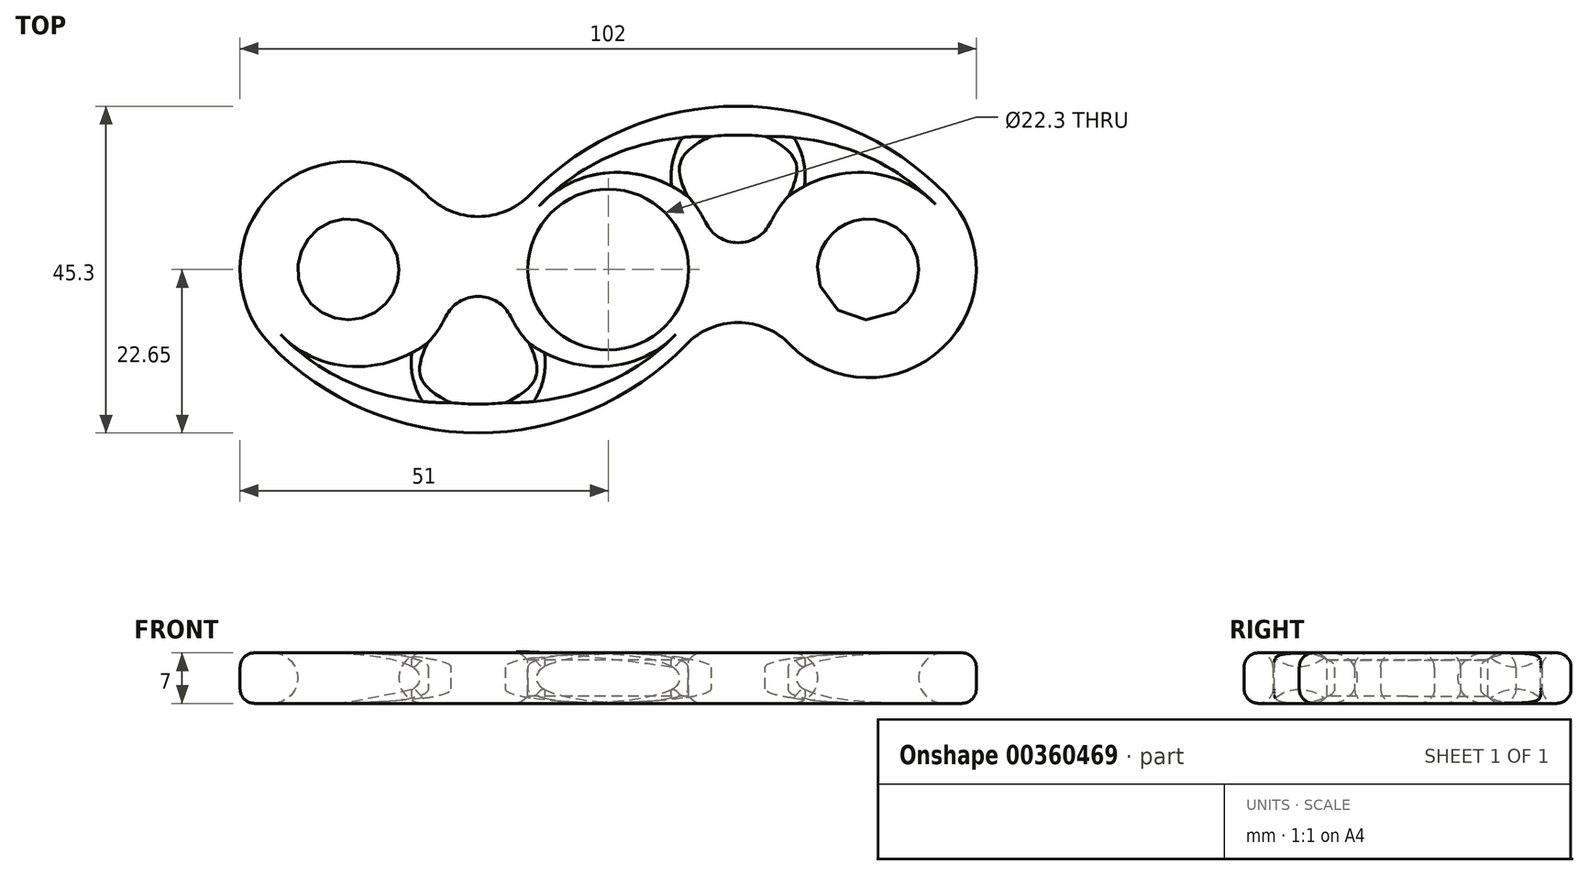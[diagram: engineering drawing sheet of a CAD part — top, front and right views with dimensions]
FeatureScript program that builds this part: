
annotation { "Feature Type Name" : "Feature", "Feature Type Description" : "" }
export const myFeature = defineFeature(function(context is Context, id is Id, definition is map)
    precondition{}
    {
        {
            var Q0;
            Q0=qCreatedBy(makeId("Top.planeOp"),FACE);
            var sketch = newSketch(context, id + "F0", { "sketchPlane" : qUnion([Q0])});
            skLineSegment(sketch, "E0", {"start": v(10.8, -10.4) * mm, "end": v(10.8, -10.4) * mm});
            skArc(sketch, "E1", {"start": v(-34.05, -14.87) * mm, "mid": v(-27.22, -12.16) * mm, "end": v(-22.5, -6.54) * mm});
            skArc(sketch, "E2", {"start": v(25.2, -10.4) * mm, "mid": v(46.4, -10.8) * mm, "end": v(46.8, 10.4) * mm});
            skArc(sketch, "E3", {"start": v(-46.8, -10.4) * mm, "mid": v(-18, -22.65) * mm, "end": v(10.8, -10.4) * mm});
            skArc(sketch, "E4", {"start": v(46.8, 10.4) * mm, "mid": v(18, 22.65) * mm, "end": v(-10.8, 10.4) * mm});
            skArc(sketch, "E5.0", {"start": v(-34.05, -14.87) * mm, "mid": v(-18, -18.65) * mm, "end": v(-1.95, -14.87) * mm});
            skArc(sketch, "E6.0", {"start": v(34.05, 14.87) * mm, "mid": v(18, 18.65) * mm, "end": v(1.95, 14.87) * mm});
            skArc(sketch, "E7", {"start": v(-25.2, 10.4) * mm, "mid": v(-18, 7.35) * mm, "end": v(-10.8, 10.4) * mm});
            skArc(sketch, "E8", {"start": v(-13.5, -6.54) * mm, "mid": v(-18, -3.72) * mm, "end": v(-22.5, -6.54) * mm});
            skArc(sketch, "E9", {"start": v(13.5, 6.54) * mm, "mid": v(18, 3.72) * mm, "end": v(22.5, 6.54) * mm});
            skArc(sketch, "E10", {"start": v(25.2, -10.4) * mm, "mid": v(18, -7.35) * mm, "end": v(10.8, -10.4) * mm});
            skArc(sketch, "E11.trimOffspring", {"start": v(-25.2, 10.4) * mm, "mid": v(-46.4, 10.8) * mm, "end": v(-46.8, -10.4) * mm});
            skArc(sketch, "E12.trimOffspring", {"start": v(-13.5, -6.54) * mm, "mid": v(-8.78, -12.16) * mm, "end": v(-1.95, -14.87) * mm});
            skArc(sketch, "E13.trimOffspring", {"start": v(13.5, 6.54) * mm, "mid": v(8.78, 12.16) * mm, "end": v(1.95, 14.87) * mm});
            skArc(sketch, "E14.trimOffspring", {"start": v(34.05, 14.87) * mm, "mid": v(27.22, 12.16) * mm, "end": v(22.5, 6.54) * mm});
            skLineSegment(sketch, "E15.trimOffspring", {"start": v(-10.8, 10.4) * mm, "end": v(-10.8, 10.4) * mm});
            skSolve(sketch);
        }
        {
            var Q0;
            Q0 = qSketchRegion(id + "F0", true);
            extrude(context, id + "F1", {"entities" : qUnion([Q0]), "depth" : 7 * mm});
        }
        {
            var Q0;
            Q0=makeQuery(id+"F1.opExtrude","CAP_FACE",FACE,{"disambiguationData":[OSD([sQuery(id+"F0.wireOp",EDGE,"E0"),sQuery(id+"F0.wireOp",EDGE,"E1"),sQuery(id+"F0.wireOp",EDGE,"E2"),sQuery(id+"F0.wireOp",EDGE,"E3"),sQuery(id+"F0.wireOp",EDGE,"E4"),sQuery(id+"F0.wireOp",EDGE,"E5.0"),sQuery(id+"F0.wireOp",EDGE,"E6.0"),sQuery(id+"F0.wireOp",EDGE,"E7"),sQuery(id+"F0.wireOp",EDGE,"E8"),sQuery(id+"F0.wireOp",EDGE,"E9"),sQuery(id+"F0.wireOp",EDGE,"E10"),sQuery(id+"F0.wireOp",EDGE,"E11.trimOffspring"),sQuery(id+"F0.wireOp",EDGE,"E12.trimOffspring"),sQuery(id+"F0.wireOp",EDGE,"E13.trimOffspring"),sQuery(id+"F0.wireOp",EDGE,"E14.trimOffspring"),sQuery(id+"F0.wireOp",EDGE,"E15.trimOffspring")])],"isStart":false});
            var sketch = newSketch(context, id + "F2", { "sketchPlane" : qUnion([Q0])});
            skCircle(sketch, "E16", {"center": v(0, 0) * mm, "radius": 11.15 * mm});
            skCircle(sketch, "E17", {"center": v(36, 0) * mm, "radius": 7 * mm});
            skCircle(sketch, "E18", {"center": v(-36, 0) * mm, "radius": 7 * mm});
            skSolve(sketch);
        }
        {
            var Q0;
            Q0 = qSketchRegion(id + "F2", true);
            extrude(context, id + "F3", {"entities" : qUnion([Q0]), "operationType" : NewBodyOperationType.REMOVE, "endBound" : BoundingType.THROUGH_ALL, "oppositeDirection" : true, "depth" : 25 * mm});
        }
        {
            var Q0;
            Q0=makeQuery(id+"F3.boolean.opBoolean","COPY",FACE,{"derivedFrom":makeQuery(id+"F3.opExtrude","SWEPT_FACE",FACE,{"disambiguationData":[OSD([sQuery(id+"F2.wireOp",EDGE,"E16")])]})});
            chamfer(context, id + "F4", {"entities" : qUnion([Q0]), "width" : 1 * mm, "tangentPropagation" : true});
        }
        {
            var Q0;
            Q0=makeQuery(id+"F3.boolean.opBoolean","COPY",FACE,{"derivedFrom":makeQuery(id+"F3.opExtrude","SWEPT_FACE",FACE,{"disambiguationData":[OSD([sQuery(id+"F2.wireOp",EDGE,"E18")])]})});
            var Q1;
            Q1=makeQuery(id+"F3.boolean.opBoolean","COPY",FACE,{"derivedFrom":makeQuery(id+"F3.opExtrude","SWEPT_FACE",FACE,{"disambiguationData":[OSD([sQuery(id+"F2.wireOp",EDGE,"E17")])]})});
            fillet(context, id + "F5", {"entities" : qUnion([Q0, Q1]), "radius" : 3.5 * mm, "tangentPropagation" : true, "allowEdgeOverflow" : false});
        }
        {
            var Q0;
            Q0=makeQuery(id+"F1.opExtrude","CAP_FACE",FACE,{"disambiguationData":[OSD([sQuery(id+"F0.wireOp",EDGE,"E0"),sQuery(id+"F0.wireOp",EDGE,"E1"),sQuery(id+"F0.wireOp",EDGE,"E2"),sQuery(id+"F0.wireOp",EDGE,"E3"),sQuery(id+"F0.wireOp",EDGE,"E4"),sQuery(id+"F0.wireOp",EDGE,"E5.0"),sQuery(id+"F0.wireOp",EDGE,"E6.0"),sQuery(id+"F0.wireOp",EDGE,"E7"),sQuery(id+"F0.wireOp",EDGE,"E8"),sQuery(id+"F0.wireOp",EDGE,"E9"),sQuery(id+"F0.wireOp",EDGE,"E10"),sQuery(id+"F0.wireOp",EDGE,"E11.trimOffspring"),sQuery(id+"F0.wireOp",EDGE,"E12.trimOffspring"),sQuery(id+"F0.wireOp",EDGE,"E13.trimOffspring"),sQuery(id+"F0.wireOp",EDGE,"E14.trimOffspring"),sQuery(id+"F0.wireOp",EDGE,"E15.trimOffspring")])],"isStart":false});
            var Q1;
            Q1=makeQuery(id+"F1.opExtrude","CAP_FACE",FACE,{"disambiguationData":[OSD([sQuery(id+"F0.wireOp",EDGE,"E0"),sQuery(id+"F0.wireOp",EDGE,"E1"),sQuery(id+"F0.wireOp",EDGE,"E2"),sQuery(id+"F0.wireOp",EDGE,"E3"),sQuery(id+"F0.wireOp",EDGE,"E4"),sQuery(id+"F0.wireOp",EDGE,"E5.0"),sQuery(id+"F0.wireOp",EDGE,"E6.0"),sQuery(id+"F0.wireOp",EDGE,"E7"),sQuery(id+"F0.wireOp",EDGE,"E8"),sQuery(id+"F0.wireOp",EDGE,"E9"),sQuery(id+"F0.wireOp",EDGE,"E10"),sQuery(id+"F0.wireOp",EDGE,"E11.trimOffspring"),sQuery(id+"F0.wireOp",EDGE,"E12.trimOffspring"),sQuery(id+"F0.wireOp",EDGE,"E13.trimOffspring"),sQuery(id+"F0.wireOp",EDGE,"E14.trimOffspring"),sQuery(id+"F0.wireOp",EDGE,"E15.trimOffspring")])],"isStart":true});
            fillet(context, id + "F6", {"entities" : qUnion([Q0, Q1]), "radius" : 2 * mm, "tangentPropagation" : true, "allowEdgeOverflow" : false});
        }
        {
            var Q0;
            Q0=makeQuery(id+"F1.opExtrude","SWEPT_EDGE",EDGE,{"disambiguationData":[OSD([sQuery(id+"F0.wireOp",EDGE,"E1"),sQuery(id+"F0.wireOp",EDGE,"E5.0")])]});
            var Q1;
            Q1=makeQuery(id+"F1.opExtrude","SWEPT_EDGE",EDGE,{"disambiguationData":[OSD([sQuery(id+"F0.wireOp",EDGE,"E5.0"),sQuery(id+"F0.wireOp",EDGE,"E12.trimOffspring")])]});
            var Q2;
            Q2=makeQuery(id+"F1.opExtrude","SWEPT_EDGE",EDGE,{"disambiguationData":[OSD([sQuery(id+"F0.wireOp",EDGE,"E6.0"),sQuery(id+"F0.wireOp",EDGE,"E14.trimOffspring")])]});
            var Q3;
            Q3=makeQuery(id+"F1.opExtrude","SWEPT_EDGE",EDGE,{"disambiguationData":[OSD([sQuery(id+"F0.wireOp",EDGE,"E6.0"),sQuery(id+"F0.wireOp",EDGE,"E13.trimOffspring")])]});
            fillet(context, id + "F7", {"entities" : qUnion([Q0, Q1, Q2, Q3]), "radius" : 5 * mm, "tangentPropagation" : true, "allowEdgeOverflow" : false});
        }
    });
